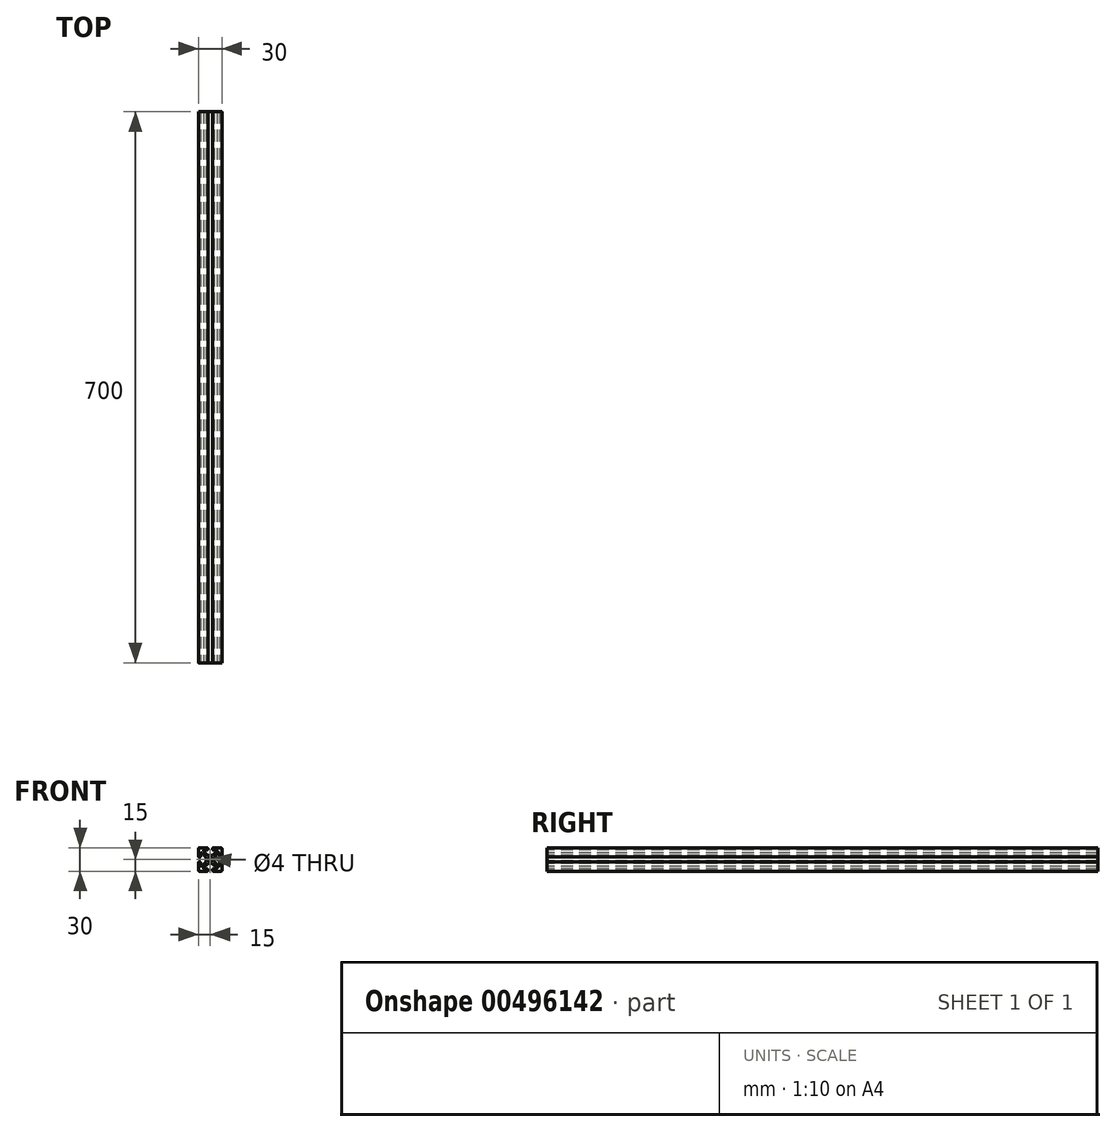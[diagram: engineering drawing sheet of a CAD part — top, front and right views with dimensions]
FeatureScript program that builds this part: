
annotation { "Feature Type Name" : "Feature", "Feature Type Description" : "" }
export const myFeature = defineFeature(function(context is Context, id is Id, definition is map)
    precondition{}
    {
        {
            var Q0;
            Q0=qCreatedBy(makeId("Front.planeOp"),FACE);
            var sketch = newSketch(context, id + "F0", { "sketchPlane" : qUnion([Q0])});
            skLineSegment(sketch, "E0.bottom", {"start": v(13.5, 15) * mm, "end": v(4, 15) * mm});
            skLineSegment(sketch, "E0.top", {"start": v(13.5, -15) * mm, "end": v(4, -15) * mm});
            skLineSegment(sketch, "E0.left", {"start": v(15, 13.5) * mm, "end": v(15, 4) * mm});
            skLineSegment(sketch, "E0.right", {"start": v(-15, 13.5) * mm, "end": v(-15, 4) * mm});
            skPoint(sketch, "E0.middle", {"position": v(0, 0) * mm});
            skLineSegment(sketch, "E1.bottom", {"start": v(7.46, 12) * mm, "end": v(4, 12) * mm});
            skLineSegment(sketch, "E1.top", {"start": v(7.46, -12) * mm, "end": v(4, -12) * mm});
            skLineSegment(sketch, "E1.left", {"start": v(12, 7.46) * mm, "end": v(12, 4) * mm});
            skLineSegment(sketch, "E1.right", {"start": v(-12, 7.46) * mm, "end": v(-12, 4) * mm});
            skLineSegment(sketch, "E2", {"start": v(8.17, 10.3) * mm, "end": v(3.32, 5.44) * mm});
            skLineSegment(sketch, "E3", {"start": v(-8.17, -10.3) * mm, "end": v(-3.32, -5.44) * mm});
            skLineSegment(sketch, "E4", {"start": v(-8.17, 10.3) * mm, "end": v(-3.32, 5.44) * mm});
            skLineSegment(sketch, "E5", {"start": v(-10.3, 8.17) * mm, "end": v(-5, 2.88) * mm});
            skPoint(sketch, "E6.orphan", {"position": v(12, 12) * mm});
            skPoint(sketch, "E7.orphan", {"position": v(12, -12) * mm});
            skPoint(sketch, "E8.orphan", {"position": v(-12, -12) * mm});
            skPoint(sketch, "E9.orphan", {"position": v(-12, 12) * mm});
            skLineSegment(sketch, "E10.trimOffspring", {"start": v(-5.44, -3.32) * mm, "end": v(-10.3, -8.17) * mm});
            skLineSegment(sketch, "E11.trimOffspring", {"start": v(5.44, -3.32) * mm, "end": v(10.3, -8.17) * mm});
            skLineSegment(sketch, "E12.trimOffspring", {"start": v(5.44, 3.32) * mm, "end": v(10.3, 8.17) * mm});
            skLineSegment(sketch, "E13.trimOffspring", {"start": v(3.32, -5.44) * mm, "end": v(8.17, -10.3) * mm});
            skLineSegment(sketch, "E14.bottom", {"start": v(2.26, 5) * mm, "end": v(-2.26, 5) * mm});
            skLineSegment(sketch, "E14.top", {"start": v(2.26, -5) * mm, "end": v(-2.26, -5) * mm});
            skLineSegment(sketch, "E14.left", {"start": v(5, 2.26) * mm, "end": v(5, -2.26) * mm});
            skLineSegment(sketch, "E14.right", {"start": v(-5, 2.88) * mm, "end": v(-5, -2.26) * mm});
            skPoint(sketch, "E15.orphan", {"position": v(5, 5) * mm});
            skPoint(sketch, "E16.orphan", {"position": v(5, -5) * mm});
            skPoint(sketch, "E17.orphan", {"position": v(-5, -5) * mm});
            skPoint(sketch, "E18.orphan", {"position": v(-5, 5) * mm});
            skCircle(sketch, "E19", {"center": v(0, 0) * mm, "radius": 2 * mm});
            skLineSegment(sketch, "E20", {"start": v(-3, 14) * mm, "end": v(-3, 13) * mm});
            skLineSegment(sketch, "E21", {"start": v(3, 14) * mm, "end": v(3, 13) * mm});
            skLineSegment(sketch, "E22.trimOffspring", {"start": v(-3, -13) * mm, "end": v(-3, -14) * mm});
            skLineSegment(sketch, "E23.trimOffspring", {"start": v(-4, 12) * mm, "end": v(-7.46, 12) * mm});
            skLineSegment(sketch, "E24.trimOffspring", {"start": v(-4, 15) * mm, "end": v(-13.5, 15) * mm});
            skLineSegment(sketch, "E25.trimOffspring", {"start": v(3, -13) * mm, "end": v(3, -14) * mm});
            skLineSegment(sketch, "E26.trimOffspring", {"start": v(-4, -12) * mm, "end": v(-7.46, -12) * mm});
            skLineSegment(sketch, "E27.trimOffspring", {"start": v(-4, -15) * mm, "end": v(-13.5, -15) * mm});
            skLineSegment(sketch, "E28", {"start": v(-14, 3) * mm, "end": v(-13, 3) * mm});
            skLineSegment(sketch, "E29", {"start": v(-14, -3) * mm, "end": v(-13, -3) * mm});
            skLineSegment(sketch, "E30.trimOffspring", {"start": v(-12, -4) * mm, "end": v(-12, -7.46) * mm});
            skLineSegment(sketch, "E31.trimOffspring", {"start": v(-15, -4) * mm, "end": v(-15, -13.5) * mm});
            skLineSegment(sketch, "E32.trimOffspring", {"start": v(13, 3) * mm, "end": v(14, 3) * mm});
            skLineSegment(sketch, "E33.trimOffspring", {"start": v(13, -3) * mm, "end": v(14, -3) * mm});
            skLineSegment(sketch, "E34.trimOffspring", {"start": v(12, -4) * mm, "end": v(12, -7.46) * mm});
            skLineSegment(sketch, "E35.trimOffspring", {"start": v(15, -4) * mm, "end": v(15, -13.5) * mm});
            skPoint(sketch, "E36.visualSharp", {"position": v(-15, 15) * mm});
            skArc(sketch, "E36.filletArc", {"start": v(-13.5, 15) * mm, "mid": v(-14.56, 14.56) * mm, "end": v(-15, 13.5) * mm});
            skPoint(sketch, "E37.visualSharp", {"position": v(15, 15) * mm});
            skArc(sketch, "E37.filletArc", {"start": v(15, 13.5) * mm, "mid": v(14.56, 14.56) * mm, "end": v(13.5, 15) * mm});
            skPoint(sketch, "E38.visualSharp", {"position": v(15, -15) * mm});
            skArc(sketch, "E38.filletArc", {"start": v(13.5, -15) * mm, "mid": v(14.56, -14.56) * mm, "end": v(15, -13.5) * mm});
            skPoint(sketch, "E39.visualSharp", {"position": v(-15, -15) * mm});
            skArc(sketch, "E39.filletArc", {"start": v(-15, -13.5) * mm, "mid": v(-14.56, -14.56) * mm, "end": v(-13.5, -15) * mm});
            skPoint(sketch, "E40.visualSharp", {"position": v(-5, -2.88) * mm});
            skArc(sketch, "E40.filletArc", {"start": v(-5.44, -3.32) * mm, "mid": v(-5.11, -2.83) * mm, "end": v(-5, -2.26) * mm});
            skPoint(sketch, "E41.visualSharp", {"position": v(-2.88, -5) * mm});
            skArc(sketch, "E41.filletArc", {"start": v(-2.26, -5) * mm, "mid": v(-2.83, -5.11) * mm, "end": v(-3.32, -5.44) * mm});
            skPoint(sketch, "E42.visualSharp", {"position": v(2.88, -5) * mm});
            skArc(sketch, "E42.filletArc", {"start": v(3.32, -5.44) * mm, "mid": v(2.83, -5.11) * mm, "end": v(2.26, -5) * mm});
            skPoint(sketch, "E43.visualSharp", {"position": v(5, -2.88) * mm});
            skArc(sketch, "E43.filletArc", {"start": v(5, -2.26) * mm, "mid": v(5.11, -2.83) * mm, "end": v(5.44, -3.32) * mm});
            skPoint(sketch, "E44.visualSharp", {"position": v(5, 2.88) * mm});
            skArc(sketch, "E44.filletArc", {"start": v(5.44, 3.32) * mm, "mid": v(5.11, 2.83) * mm, "end": v(5, 2.26) * mm});
            skPoint(sketch, "E45.visualSharp", {"position": v(2.88, 5) * mm});
            skArc(sketch, "E45.filletArc", {"start": v(2.26, 5) * mm, "mid": v(2.83, 5.11) * mm, "end": v(3.32, 5.44) * mm});
            skPoint(sketch, "E46.visualSharp", {"position": v(-2.88, 5) * mm});
            skArc(sketch, "E46.filletArc", {"start": v(-3.32, 5.44) * mm, "mid": v(-2.83, 5.11) * mm, "end": v(-2.26, 5) * mm});
            skPoint(sketch, "E47.visualSharp", {"position": v(-3, 12) * mm});
            skArc(sketch, "E47.filletArc", {"start": v(-4, 12) * mm, "mid": v(-3.3, 12.3) * mm, "end": v(-3, 13) * mm});
            skPoint(sketch, "E48.visualSharp", {"position": v(-3, 15) * mm});
            skArc(sketch, "E48.filletArc", {"start": v(-3, 14) * mm, "mid": v(-3.3, 14.7) * mm, "end": v(-4, 15) * mm});
            skPoint(sketch, "E49.visualSharp", {"position": v(3, 15) * mm});
            skArc(sketch, "E49.filletArc", {"start": v(4, 15) * mm, "mid": v(3.3, 14.7) * mm, "end": v(3, 14) * mm});
            skPoint(sketch, "E50.visualSharp", {"position": v(3, 12) * mm});
            skArc(sketch, "E50.filletArc", {"start": v(3, 13) * mm, "mid": v(3.3, 12.3) * mm, "end": v(4, 12) * mm});
            skPoint(sketch, "E51.visualSharp", {"position": v(12, 3) * mm});
            skArc(sketch, "E51.filletArc", {"start": v(12, 4) * mm, "mid": v(12.3, 3.3) * mm, "end": v(13, 3) * mm});
            skPoint(sketch, "E52.visualSharp", {"position": v(15, 3) * mm});
            skArc(sketch, "E52.filletArc", {"start": v(14, 3) * mm, "mid": v(14.7, 3.3) * mm, "end": v(15, 4) * mm});
            skPoint(sketch, "E53.visualSharp", {"position": v(15, -3) * mm});
            skArc(sketch, "E53.filletArc", {"start": v(15, -4) * mm, "mid": v(14.7, -3.3) * mm, "end": v(14, -3) * mm});
            skPoint(sketch, "E54.visualSharp", {"position": v(12, -3) * mm});
            skArc(sketch, "E54.filletArc", {"start": v(13, -3) * mm, "mid": v(12.3, -3.3) * mm, "end": v(12, -4) * mm});
            skPoint(sketch, "E55.visualSharp", {"position": v(3, -12) * mm});
            skArc(sketch, "E55.filletArc", {"start": v(4, -12) * mm, "mid": v(3.3, -12.3) * mm, "end": v(3, -13) * mm});
            skPoint(sketch, "E56.visualSharp", {"position": v(3, -15) * mm});
            skArc(sketch, "E56.filletArc", {"start": v(3, -14) * mm, "mid": v(3.3, -14.7) * mm, "end": v(4, -15) * mm});
            skPoint(sketch, "E57.visualSharp", {"position": v(-3, -12) * mm});
            skArc(sketch, "E57.filletArc", {"start": v(-3, -13) * mm, "mid": v(-3.3, -12.3) * mm, "end": v(-4, -12) * mm});
            skPoint(sketch, "E58.visualSharp", {"position": v(-3, -15) * mm});
            skArc(sketch, "E58.filletArc", {"start": v(-4, -15) * mm, "mid": v(-3.3, -14.7) * mm, "end": v(-3, -14) * mm});
            skPoint(sketch, "E59.visualSharp", {"position": v(-12, -3) * mm});
            skArc(sketch, "E59.filletArc", {"start": v(-12, -4) * mm, "mid": v(-12.3, -3.3) * mm, "end": v(-13, -3) * mm});
            skPoint(sketch, "E60.visualSharp", {"position": v(-15, -3) * mm});
            skArc(sketch, "E60.filletArc", {"start": v(-14, -3) * mm, "mid": v(-14.7, -3.3) * mm, "end": v(-15, -4) * mm});
            skPoint(sketch, "E61.visualSharp", {"position": v(-15, 3) * mm});
            skArc(sketch, "E61.filletArc", {"start": v(-15, 4) * mm, "mid": v(-14.7, 3.3) * mm, "end": v(-14, 3) * mm});
            skPoint(sketch, "E62.visualSharp", {"position": v(-12, 3) * mm});
            skArc(sketch, "E62.filletArc", {"start": v(-13, 3) * mm, "mid": v(-12.3, 3.3) * mm, "end": v(-12, 4) * mm});
            skPoint(sketch, "E63.visualSharp", {"position": v(9.88, 12) * mm});
            skArc(sketch, "E63.filletArc", {"start": v(8.17, 10.3) * mm, "mid": v(8.39, 11.38) * mm, "end": v(7.46, 12) * mm});
            skPoint(sketch, "E64.visualSharp", {"position": v(12, 9.88) * mm});
            skArc(sketch, "E64.filletArc", {"start": v(12, 7.46) * mm, "mid": v(11.38, 8.39) * mm, "end": v(10.3, 8.17) * mm});
            skPoint(sketch, "E65.visualSharp", {"position": v(12, -9.88) * mm});
            skArc(sketch, "E65.filletArc", {"start": v(10.3, -8.17) * mm, "mid": v(11.38, -8.39) * mm, "end": v(12, -7.46) * mm});
            skPoint(sketch, "E66.visualSharp", {"position": v(9.88, -12) * mm});
            skArc(sketch, "E66.filletArc", {"start": v(7.46, -12) * mm, "mid": v(8.39, -11.38) * mm, "end": v(8.17, -10.3) * mm});
            skPoint(sketch, "E67.visualSharp", {"position": v(-12, -9.88) * mm});
            skArc(sketch, "E67.filletArc", {"start": v(-12, -7.46) * mm, "mid": v(-11.38, -8.39) * mm, "end": v(-10.3, -8.17) * mm});
            skPoint(sketch, "E68.visualSharp", {"position": v(-9.88, -12) * mm});
            skArc(sketch, "E68.filletArc", {"start": v(-8.17, -10.3) * mm, "mid": v(-8.39, -11.38) * mm, "end": v(-7.46, -12) * mm});
            skPoint(sketch, "E69.visualSharp", {"position": v(-12, 9.88) * mm});
            skArc(sketch, "E69.filletArc", {"start": v(-10.3, 8.17) * mm, "mid": v(-11.38, 8.39) * mm, "end": v(-12, 7.46) * mm});
            skPoint(sketch, "E70.visualSharp", {"position": v(-9.88, 12) * mm});
            skArc(sketch, "E70.filletArc", {"start": v(-7.46, 12) * mm, "mid": v(-8.39, 11.38) * mm, "end": v(-8.17, 10.3) * mm});
            skSolve(sketch);
        }
        {
            var Q0;
            Q0 = qSketchRegion(id + "F0", true);
            extrude(context, id + "F1", {"entities" : qUnion([Q0]), "oppositeDirection" : true, "depth" : 700 * mm});
        }
    });
